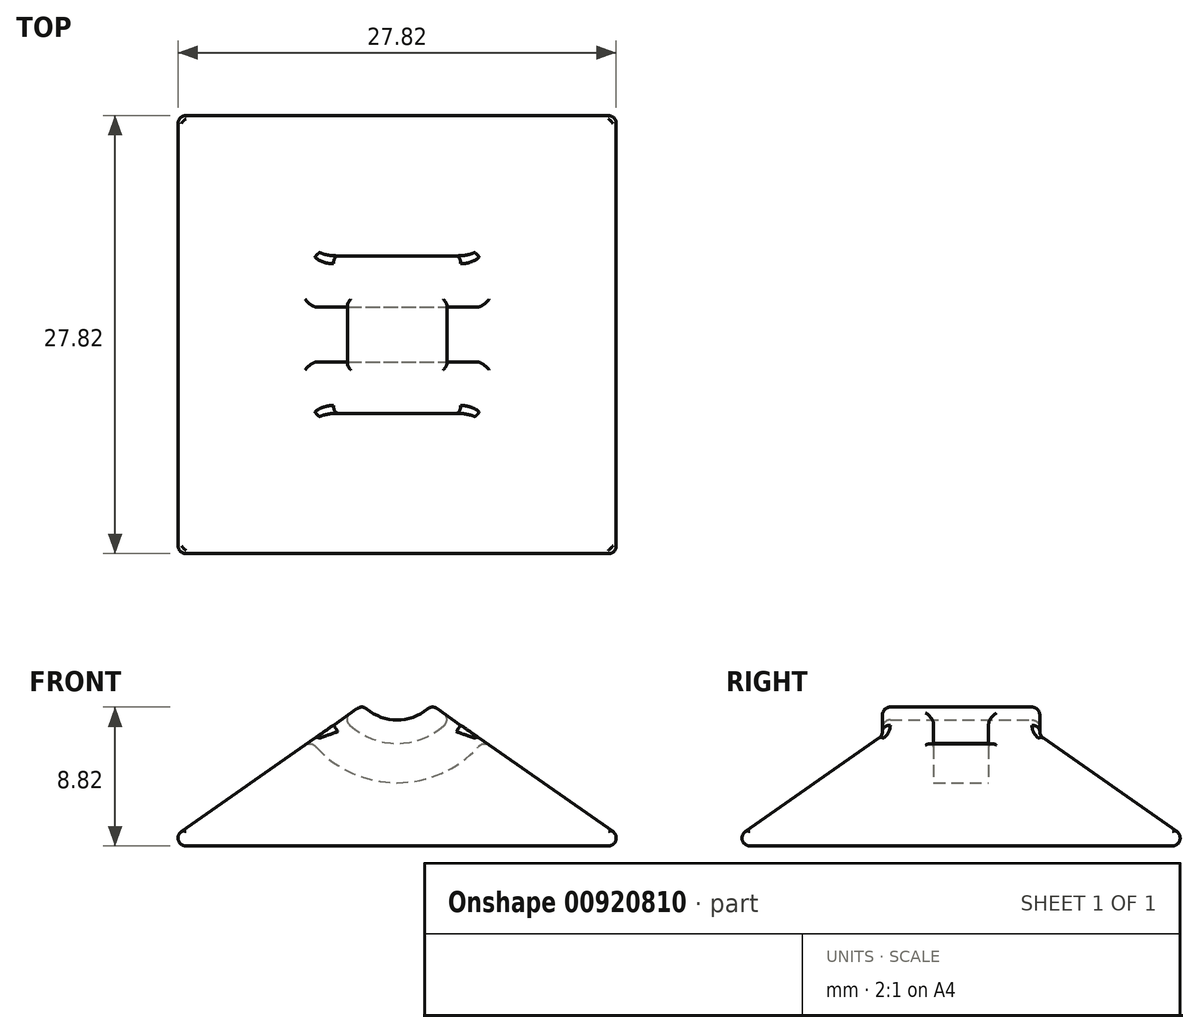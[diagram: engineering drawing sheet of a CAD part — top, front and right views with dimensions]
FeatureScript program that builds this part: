
annotation { "Feature Type Name" : "Feature", "Feature Type Description" : "" }
export const myFeature = defineFeature(function(context is Context, id is Id, definition is map)
    precondition{}
    {
        {
            var Q0;
            Q0=qCreatedBy(makeId("Top.planeOp"),FACE);
            var sketch = newSketch(context, id + "F0", { "sketchPlane" : qUnion([Q0])});
            skLineSegment(sketch, "E0.bottom", {"start": v(-15, 15) * mm, "end": v(15, 15) * mm});
            skLineSegment(sketch, "E0.top", {"start": v(-15, -15) * mm, "end": v(15, -15) * mm});
            skLineSegment(sketch, "E0.left", {"start": v(-15, 15) * mm, "end": v(-15, -15) * mm});
            skLineSegment(sketch, "E0.right", {"start": v(15, 15) * mm, "end": v(15, -15) * mm});
            skSolve(sketch);
        }
        {
            var Q0;
            Q0=qCreatedBy(makeId("Top.planeOp"),FACE);
            cPlane(context, id + "F1", {"entities" : qUnion([Q0]), "cplaneType" : CPlaneType.OFFSET, "offset" : 7 * mm, "width" : 150 * mm, "height" : 150 * mm});
        }
        {
            var Q0;
            Q0=qCreatedBy(id+"F1.planeOp",FACE);
            var sketch = newSketch(context, id + "F2", { "sketchPlane" : qUnion([Q0])});
            skLineSegment(sketch, "E1.bottom", {"start": v(-5, 5) * mm, "end": v(5, 5) * mm});
            skLineSegment(sketch, "E1.top", {"start": v(-5, -5) * mm, "end": v(5, -5) * mm});
            skLineSegment(sketch, "E1.left", {"start": v(-5, 5) * mm, "end": v(-5, -5) * mm});
            skLineSegment(sketch, "E1.right", {"start": v(5, 5) * mm, "end": v(5, -5) * mm});
            skSolve(sketch);
        }
        {
            var Q0;
            Q0 = qSketchRegion(id + "F0", true);
            var Q1;
            Q1 = qSketchRegion(id + "F2", true);
            loft(context, id + "F3", {"sheetProfilesArray" : [{ "sheetProfileEntities" : qUnion([Q0]) }, { "sheetProfileEntities" : qUnion([Q1]) }]});
        }
        {
            var Q0;
            Q0=qCreatedBy(makeId("Front.planeOp"),FACE);
            var sketch = newSketch(context, id + "F4", { "sketchPlane" : qUnion([Q0])});
            skArc(sketch, "E2", {"start": v(-2.2, 8.96) * mm, "mid": v(0, 8) * mm, "end": v(2.2, 8.96) * mm});
            skLineSegment(sketch, "E3", {"start": v(-2.2, 8.96) * mm, "end": v(-5, 7) * mm});
            skLineSegment(sketch, "E4", {"start": v(-5, 7) * mm, "end": v(5, 7) * mm});
            skLineSegment(sketch, "E5", {"start": v(5, 7) * mm, "end": v(2.2, 8.96) * mm});
            skSolve(sketch);
        }
        {
            var Q0;
            Q0 = qSketchRegion(id + "F4", true);
            var Q1;
            Q1=makeQuery(id+"F3.opLoft","SWEPT_BODY",BODY,{"disambiguationData":[OSD([makeQuery(id+"F0.imprint","IMPRINT",FACE,{"disambiguationData":[TD([[makeQuery(id+"F0.imprint","IMPRINT",EDGE,{"derivedFrom":sQuery(id+"F0.wireOp",EDGE,"E0.bottom")}),-1.0]])]}),makeQuery(id+"F2.imprint","IMPRINT",FACE,{"disambiguationData":[TD([[makeQuery(id+"F2.imprint","IMPRINT",EDGE,{"derivedFrom":sQuery(id+"F2.wireOp",EDGE,"E1.bottom")}),-1.0]])]})])]});
            extrude(context, id + "F5", {"entities" : qUnion([Q0]), "operationType" : NewBodyOperationType.ADD, "endBound" : BoundingType.SYMMETRIC, "depth" : 10 * mm, "endBoundEntityBody" : qUnion([Q1]), "offsetDistance" : 25 * mm, "hasSecondDirection" : true, "secondDirectionOppositeDirection" : true, "secondDirectionDepth" : 25 * mm});
        }
        {
            var Q0;
            Q0=qCreatedBy(makeId("Front.planeOp"),FACE);
            var sketch = newSketch(context, id + "F6", { "sketchPlane" : qUnion([Q0])});
            skArc(sketch, "E6", {"start": v(3.43, 8.1) * mm, "mid": v(0, 6.5) * mm, "end": v(-3.43, 8.1) * mm});
            skArc(sketch, "E7", {"start": v(-5.48, 6.67) * mm, "mid": v(0, 4.02) * mm, "end": v(5.48, 6.67) * mm});
            skLineSegment(sketch, "E8", {"start": v(-3.43, 8.1) * mm, "end": v(-5.48, 6.67) * mm});
            skLineSegment(sketch, "E9", {"start": v(3.43, 8.1) * mm, "end": v(5.48, 6.67) * mm});
            skSolve(sketch);
        }
        {
            var Q0;
            Q0 = qSketchRegion(id + "F6", true);
            extrude(context, id + "F7", {"entities" : qUnion([Q0]), "operationType" : NewBodyOperationType.REMOVE, "endBound" : BoundingType.SYMMETRIC, "depth" : 3.5 * mm, "offsetDistance" : 25 * mm});
        }
        {
            var Q0;
            Q0=makeQuery(id+"F5.boolean.opBoolean","MERGE",FACE,{"derivedFrom":[makeQuery(id+"F3.opLoft","SWEPT_FACE",FACE,{"disambiguationData":[OSD([sQuery(id+"F0.wireOp",EDGE,"E0.bottom"),sQuery(id+"F0.wireOp",EDGE,"E0.top"),sQuery(id+"F0.wireOp",EDGE,"E0.right"),sQuery(id+"F2.wireOp",EDGE,"E1.bottom"),sQuery(id+"F2.wireOp",EDGE,"E1.top"),sQuery(id+"F2.wireOp",EDGE,"E1.right")])]}),makeQuery(id+"F5.opExtrude","SWEPT_FACE",FACE,{"disambiguationData":[OSD([sQuery(id+"F4.wireOp",EDGE,"E5")])]})]});
            var Q1;
            Q1=makeQuery(id+"F5.boolean.opBoolean","MERGE",FACE,{"derivedFrom":[makeQuery(id+"F3.opLoft","SWEPT_FACE",FACE,{"disambiguationData":[OSD([sQuery(id+"F0.wireOp",EDGE,"E0.bottom"),sQuery(id+"F0.wireOp",EDGE,"E0.top"),sQuery(id+"F0.wireOp",EDGE,"E0.left"),sQuery(id+"F2.wireOp",EDGE,"E1.bottom"),sQuery(id+"F2.wireOp",EDGE,"E1.top"),sQuery(id+"F2.wireOp",EDGE,"E1.left")])]}),makeQuery(id+"F5.opExtrude","SWEPT_FACE",FACE,{"disambiguationData":[OSD([sQuery(id+"F4.wireOp",EDGE,"E3")])]})]});
            var Q2;
            Q2=makeQuery(id+"F3.opLoft","SWEPT_FACE",FACE,{"disambiguationData":[OSD([sQuery(id+"F0.wireOp",EDGE,"E0.top"),sQuery(id+"F0.wireOp",EDGE,"E0.left"),sQuery(id+"F0.wireOp",EDGE,"E0.right"),sQuery(id+"F2.wireOp",EDGE,"E1.top"),sQuery(id+"F2.wireOp",EDGE,"E1.left"),sQuery(id+"F2.wireOp",EDGE,"E1.right")])]});
            var Q3;
            Q3=makeQuery(id+"F3.opLoft","SWEPT_FACE",FACE,{"disambiguationData":[OSD([sQuery(id+"F0.wireOp",EDGE,"E0.bottom"),sQuery(id+"F0.wireOp",EDGE,"E0.left"),sQuery(id+"F0.wireOp",EDGE,"E0.right"),sQuery(id+"F2.wireOp",EDGE,"E1.bottom"),sQuery(id+"F2.wireOp",EDGE,"E1.left"),sQuery(id+"F2.wireOp",EDGE,"E1.right")])]});
            var Q4;
            Q4=makeQuery(id+"F5.opExtrude","SWEPT_FACE",FACE,{"disambiguationData":[OSD([sQuery(id+"F4.wireOp",EDGE,"E2")])]});
            fillet(context, id + "F8", {"entities" : qUnion([Q0, Q1, Q2, Q3, Q4]), "radius" : 0.5 * mm, "tangentPropagation" : true, "allowEdgeOverflow" : false});
        }
    });
